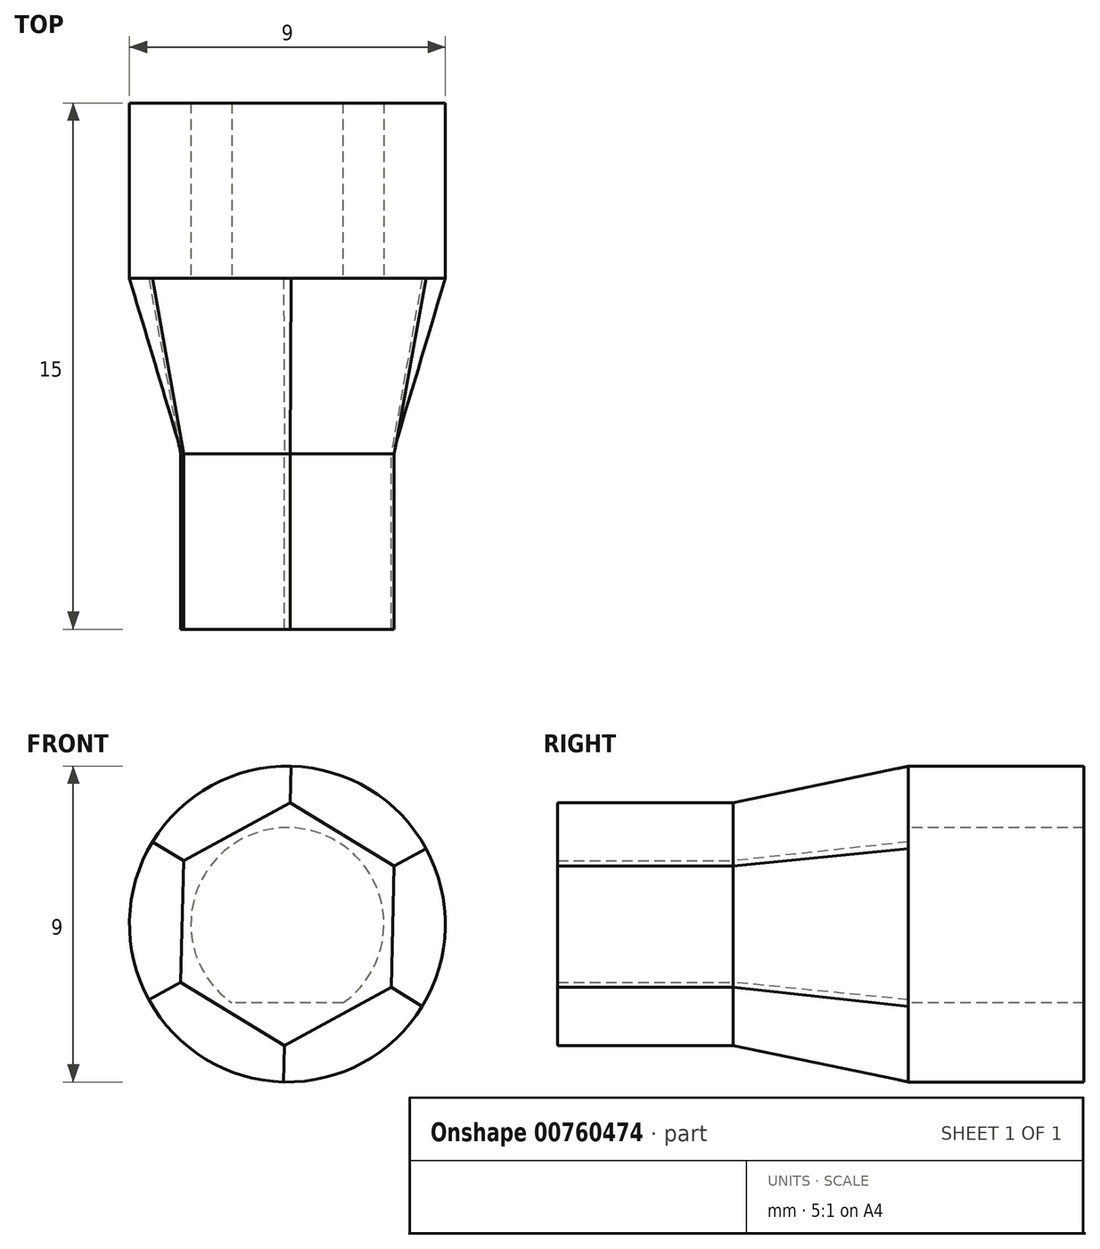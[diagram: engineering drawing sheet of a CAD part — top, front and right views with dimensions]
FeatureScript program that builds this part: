
annotation { "Feature Type Name" : "Feature", "Feature Type Description" : "" }
export const myFeature = defineFeature(function(context is Context, id is Id, definition is map)
    precondition{}
    {
        {
            var Q0;
            Q0=qCreatedBy(makeId("Front.planeOp"),FACE);
            var sketch = newSketch(context, id + "F0", { "sketchPlane" : qUnion([Q0])});
            skCircle(sketch, "E0", {"center": v(0, 0) * mm, "radius": 4.5 * mm});
            skSolve(sketch);
        }
        {
            var Q0;
            Q0=qCreatedBy(makeId("Front.planeOp"),FACE);
            cPlane(context, id + "F1", {"entities" : qUnion([Q0]), "cplaneType" : CPlaneType.OFFSET, "offset" : 5 * mm, "width" : 150 * mm, "height" : 150 * mm});
        }
        {
            var Q0;
            Q0=qCreatedBy(id+"F1.planeOp",FACE);
            var sketch = newSketch(context, id + "F2", { "sketchPlane" : qUnion([Q0])});
            skCircle(sketch, "E1.cCircle", {"center": v(0, 0) * mm, "radius": 3 * mm, "construction": true});
            skLineSegment(sketch, "E1.0", {"start": v(3.04, 1.66) * mm, "end": v(2.96, -1.8) * mm});
            skLineSegment(sketch, "E1.1", {"start": v(2.96, -1.8) * mm, "end": v(-0.08, -3.46) * mm});
            skLineSegment(sketch, "E1.2", {"start": v(-0.08, -3.46) * mm, "end": v(-3.04, -1.66) * mm});
            skLineSegment(sketch, "E1.3", {"start": v(-3.04, -1.66) * mm, "end": v(-2.96, 1.8) * mm});
            skLineSegment(sketch, "E1.4", {"start": v(-2.96, 1.8) * mm, "end": v(0.08, 3.46) * mm});
            skLineSegment(sketch, "E1.5", {"start": v(0.08, 3.46) * mm, "end": v(3.04, 1.66) * mm});
            skPoint(sketch, "E1.0.midPoint", {"position": v(3, -0.07) * mm});
            skSolve(sketch);
        }
        {
            var Q0;
            Q0=makeQuery(id+"F0.imprint","IMPRINT",FACE,{"disambiguationData":[TD([[makeQuery(id+"F0.imprint","IMPRINT",EDGE,{"derivedFrom":sQuery(id+"F0.wireOp",EDGE,"E0")}),1.0]])]});
            var Q1;
            Q1=makeQuery(id+"F2.imprint","IMPRINT",FACE,{"disambiguationData":[TD([[makeQuery(id+"F2.imprint","IMPRINT",EDGE,{"derivedFrom":sQuery(id+"F2.wireOp",EDGE,"E1.0")}),-1.0]])]});
            loft(context, id + "F3", {"sheetProfilesArray" : [{ "sheetProfileEntities" : qUnion([Q0]) }, { "sheetProfileEntities" : qUnion([Q1]) }]});
        }
        {
            var Q0;
            Q0=makeQuery(id+"F3.opLoft","CAP_FACE",FACE,{"disambiguationData":[OSD([makeQuery(id+"F0.imprint","IMPRINT",FACE,{"disambiguationData":[TD([[makeQuery(id+"F0.imprint","IMPRINT",EDGE,{"derivedFrom":sQuery(id+"F0.wireOp",EDGE,"E0")}),1.0]])]})])],"isStart":true});
            extrude(context, id + "F4", {"entities" : qUnion([Q0]), "operationType" : NewBodyOperationType.ADD, "depth" : 5 * mm, "offsetDistance" : 25 * mm});
        }
        {
            var Q0;
            Q0=makeQuery(id+"F3.opLoft","CAP_FACE",FACE,{"disambiguationData":[OSD([makeQuery(id+"F2.imprint","IMPRINT",FACE,{"disambiguationData":[TD([[makeQuery(id+"F2.imprint","IMPRINT",EDGE,{"derivedFrom":sQuery(id+"F2.wireOp",EDGE,"E1.0")}),-1.0]])]})])],"isStart":true});
            extrude(context, id + "F5", {"entities" : qUnion([Q0]), "operationType" : NewBodyOperationType.ADD, "depth" : 5 * mm, "offsetDistance" : 25 * mm});
        }
        {
            var Q0;
            Q0=qCreatedBy(makeId("Front.planeOp"),FACE);
            var sketch = newSketch(context, id + "F6", { "sketchPlane" : qUnion([Q0])});
            skCircle(sketch, "E2", {"center": v(0, 0) * mm, "radius": 2.75 * mm});
            skLineSegment(sketch, "E3", {"start": v(1.58, -2.25) * mm, "end": v(-1.58, -2.25) * mm});
            skSolve(sketch);
        }
        {
            var Q0;
            {var subQ0=sQuery(id+"F6.wireOp",EDGE,"E3");Q0=makeQuery(id+"F6.imprint","IMPRINT",FACE,{"disambiguationData":[TD([[makeQuery(id+"F6.imprint","IMPRINT",EDGE,{"derivedFrom":subQ0}),-1.0]])]});}
            extrude(context, id + "F7", {"entities" : qUnion([Q0]), "operationType" : NewBodyOperationType.REMOVE, "oppositeDirection" : true, "depth" : 5 * mm, "offsetDistance" : 25 * mm});
        }
    });
